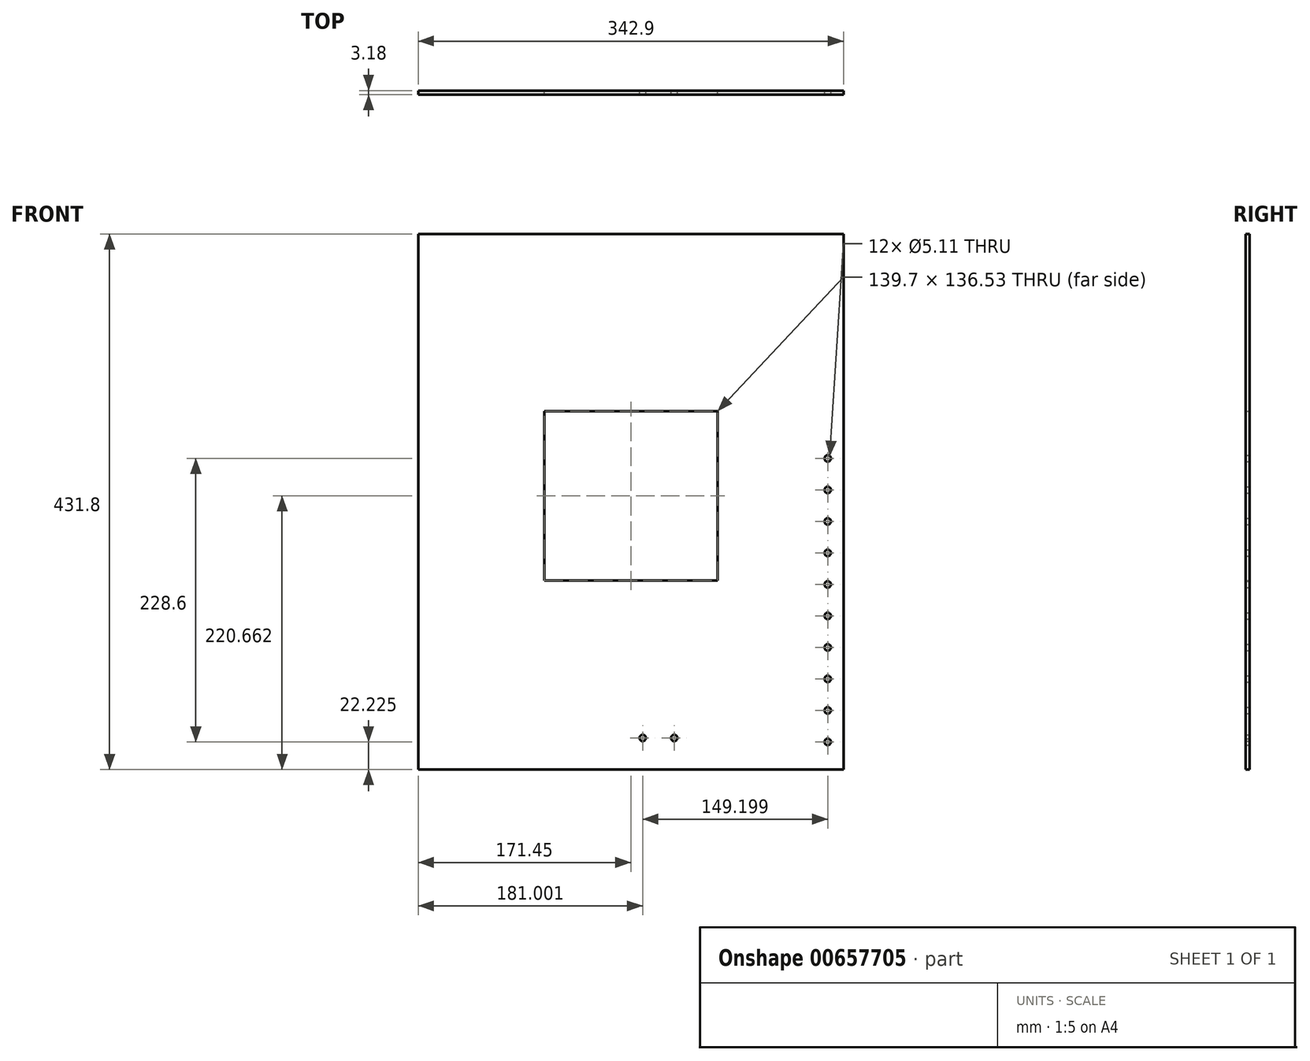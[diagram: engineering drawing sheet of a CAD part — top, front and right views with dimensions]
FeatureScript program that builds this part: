
annotation { "Feature Type Name" : "Feature", "Feature Type Description" : "" }
export const myFeature = defineFeature(function(context is Context, id is Id, definition is map)
    precondition{}
    {
        {
            var Q0;
            Q0=qCreatedBy(makeId("Front.planeOp"),FACE);
            var sketch = newSketch(context, id + "F0", { "sketchPlane" : qUnion([Q0])});
            skLineSegment(sketch, "E0.bottom", {"start": v(0, 0) * mm, "end": v(342.9, 0) * mm});
            skLineSegment(sketch, "E0.top", {"start": v(0, 431.8) * mm, "end": v(342.9, 431.8) * mm});
            skLineSegment(sketch, "E0.left", {"start": v(0, 0) * mm, "end": v(0, 431.8) * mm});
            skLineSegment(sketch, "E0.right", {"start": v(342.9, 0) * mm, "end": v(342.9, 431.8) * mm});
            skCircle(sketch, "E1", {"center": v(181, 25.4) * mm, "radius": 2.55 * mm});
            skCircle(sketch, "E2", {"center": v(206.4, 25.4) * mm, "radius": 2.55 * mm});
            skCircle(sketch, "E3", {"center": v(330.2, 22.23) * mm, "radius": 2.55 * mm});
            skCircle(sketch, "E4.0.1.0", {"center": v(330.2, 47.62) * mm, "radius": 2.55 * mm});
            skCircle(sketch, "E4.0.2.0", {"center": v(330.2, 73.03) * mm, "radius": 2.55 * mm});
            skCircle(sketch, "E4.0.3.0", {"center": v(330.2, 98.42) * mm, "radius": 2.55 * mm});
            skCircle(sketch, "E4.0.4.0", {"center": v(330.2, 123.82) * mm, "radius": 2.55 * mm});
            skCircle(sketch, "E4.0.5.0", {"center": v(330.2, 149.22) * mm, "radius": 2.55 * mm});
            skCircle(sketch, "E4.0.6.0", {"center": v(330.2, 174.62) * mm, "radius": 2.55 * mm});
            skCircle(sketch, "E4.0.7.0", {"center": v(330.2, 200.02) * mm, "radius": 2.55 * mm});
            skCircle(sketch, "E4.0.8.0", {"center": v(330.2, 225.42) * mm, "radius": 2.55 * mm});
            skCircle(sketch, "E4.0.9.0", {"center": v(330.2, 250.83) * mm, "radius": 2.55 * mm});
            skLineSegment(sketch, "E4.direction1", {"start": v(330.2, 22.23) * mm, "end": v(355.6, 22.23) * mm, "construction": true});
            skLineSegment(sketch, "E4.direction2", {"start": v(330.2, 22.23) * mm, "end": v(330.2, 47.62) * mm, "construction": true});
            skLineSegment(sketch, "E5.bottom", {"start": v(101.6, 431.8) * mm, "end": v(241.3, 431.8) * mm});
            skLineSegment(sketch, "E5.top", {"start": v(101.6, 152.4) * mm, "end": v(241.3, 152.4) * mm});
            skLineSegment(sketch, "E5.left", {"start": v(101.6, 431.8) * mm, "end": v(101.6, 152.4) * mm});
            skLineSegment(sketch, "E5.right", {"start": v(241.3, 431.8) * mm, "end": v(241.3, 152.4) * mm});
            skLineSegment(sketch, "E6.top", {"start": v(0, 288.93) * mm, "end": v(342.9, 288.93) * mm});
            skLineSegment(sketch, "E6.left", {"start": v(0, 431.8) * mm, "end": v(0, 288.93) * mm});
            skLineSegment(sketch, "E6.right", {"start": v(342.9, 431.8) * mm, "end": v(342.9, 288.93) * mm});
            skSolve(sketch);
        }
        {
            var Q0;
            {var subQ0=sQuery(id+"F0.wireOp",EDGE,"E0.top");Q0=makeQuery(id+"F0.imprint","IMPRINT",FACE,{"disambiguationData":[TD([[makeQuery(id+"F0.imprint","IMPRINT",EDGE,{"derivedFrom":subQ0}),-1.0]])]});}
            var Q1;
            {var subQ0=sQuery(id+"F0.wireOp",EDGE,"E0.bottom");Q1=makeQuery(id+"F0.imprint","IMPRINT",FACE,{"disambiguationData":[TD([[makeQuery(id+"F0.imprint","IMPRINT",EDGE,{"derivedFrom":subQ0}),1.0]])]});}
            extrude(context, id + "F1", {"entities" : qUnion([Q0, Q1]), "depth" : 3.17 * mm, "offsetDistance" : 25.4 * mm});
        }
    });
